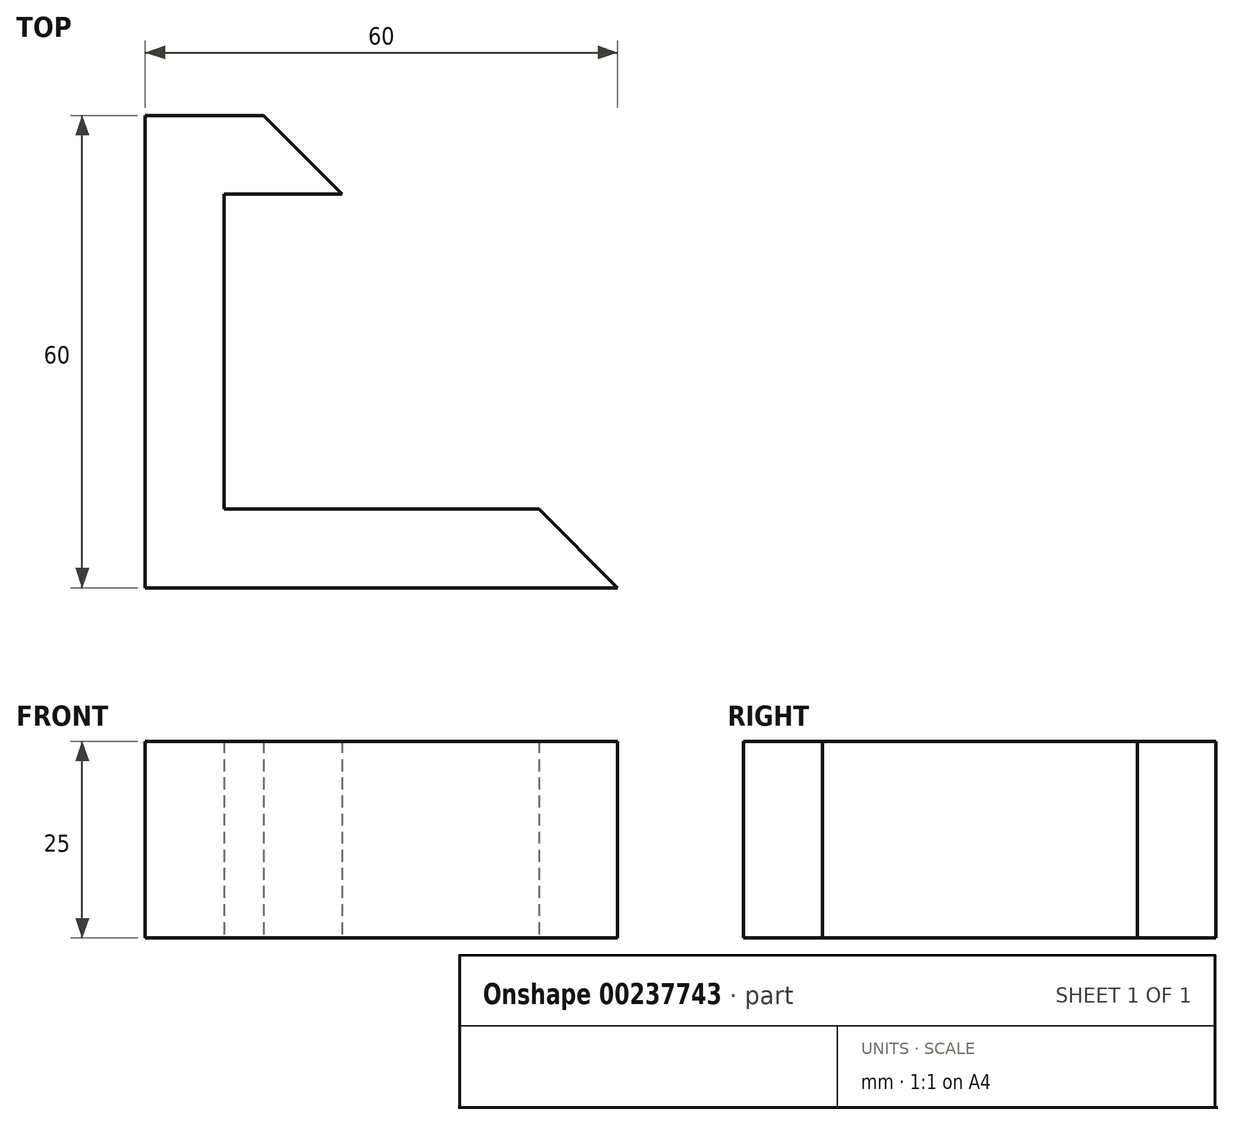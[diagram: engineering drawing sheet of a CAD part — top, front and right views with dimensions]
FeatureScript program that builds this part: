
annotation { "Feature Type Name" : "Feature", "Feature Type Description" : "" }
export const myFeature = defineFeature(function(context is Context, id is Id, definition is map)
    precondition{}
    {
        {
            var Q0;
            Q0=qCreatedBy(makeId("Top.planeOp"),FACE);
            var sketch = newSketch(context, id + "F0", { "sketchPlane" : qUnion([Q0])});
            skLineSegment(sketch, "E0", {"start": v(-35, 50) * mm, "end": v(-45, 60) * mm});
            skLineSegment(sketch, "E1", {"start": v(-45, 60) * mm, "end": v(-60, 60) * mm});
            skLineSegment(sketch, "E2", {"start": v(-60, 60) * mm, "end": v(-60, 0) * mm});
            skLineSegment(sketch, "E3", {"start": v(-60, 0) * mm, "end": v(0, 0) * mm});
            skLineSegment(sketch, "E4", {"start": v(0, 0) * mm, "end": v(-10, 10) * mm});
            skLineSegment(sketch, "E5", {"start": v(-10, 10) * mm, "end": v(-50, 10) * mm});
            skLineSegment(sketch, "E6", {"start": v(-50, 10) * mm, "end": v(-50, 50) * mm});
            skLineSegment(sketch, "E7", {"start": v(-50, 50) * mm, "end": v(-35, 50) * mm});
            skSolve(sketch);
        }
        {
            var Q0;
            Q0 = qSketchRegion(id + "F0", true);
            extrude(context, id + "F1", {"entities" : qUnion([Q0]), "depth" : 25 * mm});
        }
    });
